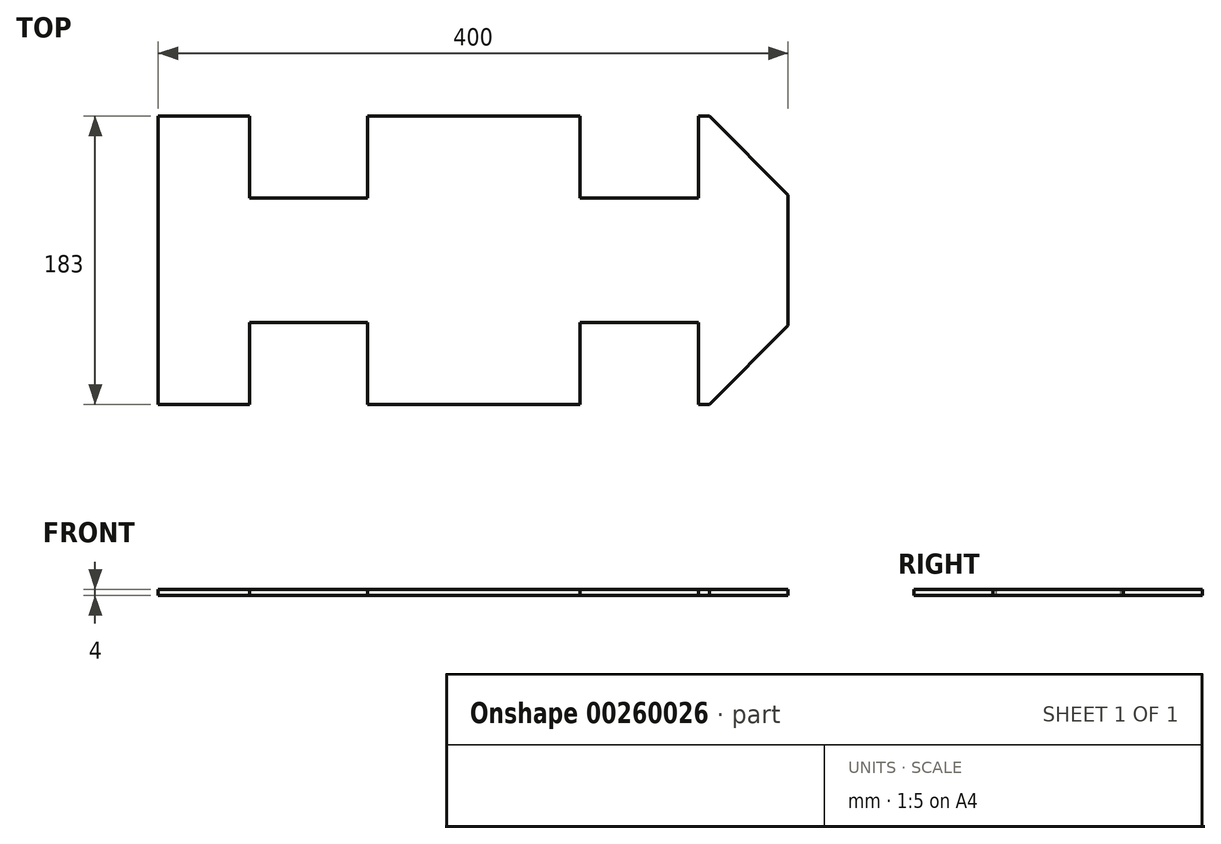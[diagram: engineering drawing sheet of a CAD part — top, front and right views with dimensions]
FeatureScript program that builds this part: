
annotation { "Feature Type Name" : "Feature", "Feature Type Description" : "" }
export const myFeature = defineFeature(function(context is Context, id is Id, definition is map)
    precondition{}
    {
        {
            var Q0;
            Q0=qCreatedBy(makeId("Top.planeOp"),FACE);
            var sketch = newSketch(context, id + "F0", { "sketchPlane" : qUnion([Q0])});
            skLineSegment(sketch, "E0", {"start": v(0, 0) * mm, "end": v(0, 91.5) * mm});
            skLineSegment(sketch, "E1", {"start": v(0, 91.5) * mm, "end": v(58, 91.5) * mm});
            skLineSegment(sketch, "E2", {"start": v(58, 91.5) * mm, "end": v(58, 39.5) * mm});
            skLineSegment(sketch, "E3", {"start": v(58, 39.5) * mm, "end": v(133, 39.5) * mm});
            skLineSegment(sketch, "E4", {"start": v(133, 39.5) * mm, "end": v(133, 91.5) * mm});
            skLineSegment(sketch, "E5", {"start": v(133, 91.5) * mm, "end": v(268, 91.5) * mm});
            skLineSegment(sketch, "E6", {"start": v(268, 91.5) * mm, "end": v(268, 39.5) * mm});
            skLineSegment(sketch, "E7", {"start": v(268, 39.5) * mm, "end": v(343, 39.5) * mm});
            skLineSegment(sketch, "E8", {"start": v(343, 39.5) * mm, "end": v(343, 91.5) * mm});
            skLineSegment(sketch, "E9", {"start": v(343, 91.5) * mm, "end": v(350, 91.5) * mm});
            skLineSegment(sketch, "E10", {"start": v(400, 41.5) * mm, "end": v(400, 0) * mm});
            skLineSegment(sketch, "E11", {"start": v(350, 91.5) * mm, "end": v(400, 41.5) * mm});
            skLineSegment(sketch, "E12.MirrorCS", {"start": v(343, -91.5) * mm, "end": v(350, -91.5) * mm});
            skLineSegment(sketch, "E13.MirrorCS", {"start": v(58, -91.5) * mm, "end": v(58, -39.5) * mm});
            skLineSegment(sketch, "E14.MirrorCS", {"start": v(58, -39.5) * mm, "end": v(133, -39.5) * mm});
            skLineSegment(sketch, "E15.MirrorCS", {"start": v(133, -39.5) * mm, "end": v(133, -91.5) * mm});
            skLineSegment(sketch, "E16.MirrorCS", {"start": v(133, -91.5) * mm, "end": v(268, -91.5) * mm});
            skLineSegment(sketch, "E17.MirrorCS", {"start": v(268, -91.5) * mm, "end": v(268, -39.5) * mm});
            skLineSegment(sketch, "E18.MirrorCS", {"start": v(268, -39.5) * mm, "end": v(343, -39.5) * mm});
            skLineSegment(sketch, "E19.MirrorCS", {"start": v(343, -39.5) * mm, "end": v(343, -91.5) * mm});
            skLineSegment(sketch, "E20.MirrorCS", {"start": v(400, -41.5) * mm, "end": v(400, 0) * mm});
            skLineSegment(sketch, "E21.MirrorCS", {"start": v(350, -91.5) * mm, "end": v(400, -41.5) * mm});
            skLineSegment(sketch, "E22.MirrorCS", {"start": v(0, 0) * mm, "end": v(0, -91.5) * mm});
            skLineSegment(sketch, "E23.MirrorCS", {"start": v(0, -91.5) * mm, "end": v(58, -91.5) * mm});
            skSolve(sketch);
        }
        {
            var Q0;
            Q0=makeQuery(id+"F0.imprint","IMPRINT",FACE,{"disambiguationData":[TD([[makeQuery(id+"F0.imprint","IMPRINT",EDGE,{"derivedFrom":sQuery(id+"F0.wireOp",EDGE,"E0")}),-1.0]])]});
            extrude(context, id + "F1", {"entities" : qUnion([Q0]), "endBound" : BoundingType.SYMMETRIC, "depth" : 4 * mm});
        }
    });
